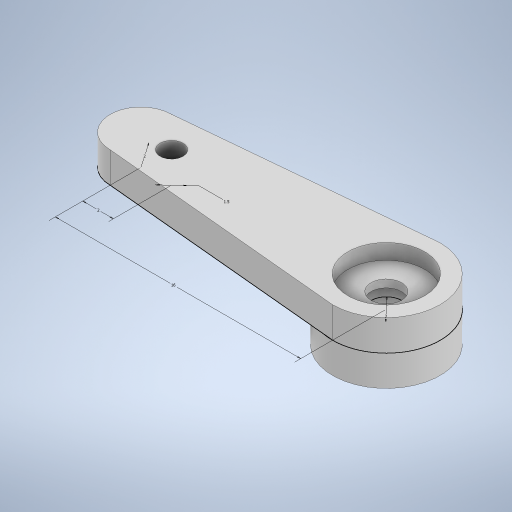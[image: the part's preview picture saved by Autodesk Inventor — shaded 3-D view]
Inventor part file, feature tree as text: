
AUTODESK INVENTOR PART (.ipt)
format: ipt  version: 2023.2 (Build 272271000, 271)  size: 295,424 bytes
history: native  units: mm
features: sketch x2
ambient origin geometry x8: Origin, YZ Plane, XZ Plane, XY Plane, X Axis, Y Axis, Z Axis, Center Point
bodies: Body1 (feature_tree)
feature tree (2):
  sketch  "Sketch2"  dims[d229=7.0mm d230=2.0mm d231=0.0mm d234=1.5mm d236=16.0mm d237=2.0mm d238=2.0mm d239=2.0mm d240=0.0mm d241=2.0mm d242=1.0mm d243=0.0mm d244=0.5mm d245=0.0mm d9=0.5mm d10=0.872665mm d11=0.5mm d12=0.872665mm d13=0.5mm d14=0.872665mm d27=0.5mm d28=0.872665mm d29=0.5mm d30=0.872665mm d88=0.5mm d89=0.872665mm d90=0.5mm d91=0.872665mm d116=0.5mm d117=0.872665mm d118=0.5mm d119=0.872665mm d154=0.5mm d155=0.872665mm d156=0.5mm d157=0.872665mm d181=0.5mm d182=0.872665mm d183=0.5mm d184=0.872665mm d221=0.5mm d222=0.872665mm d223=0.5mm d224=0.872665mm]
  sketch  "Sketch1"  dims[d228=5.0mm]
